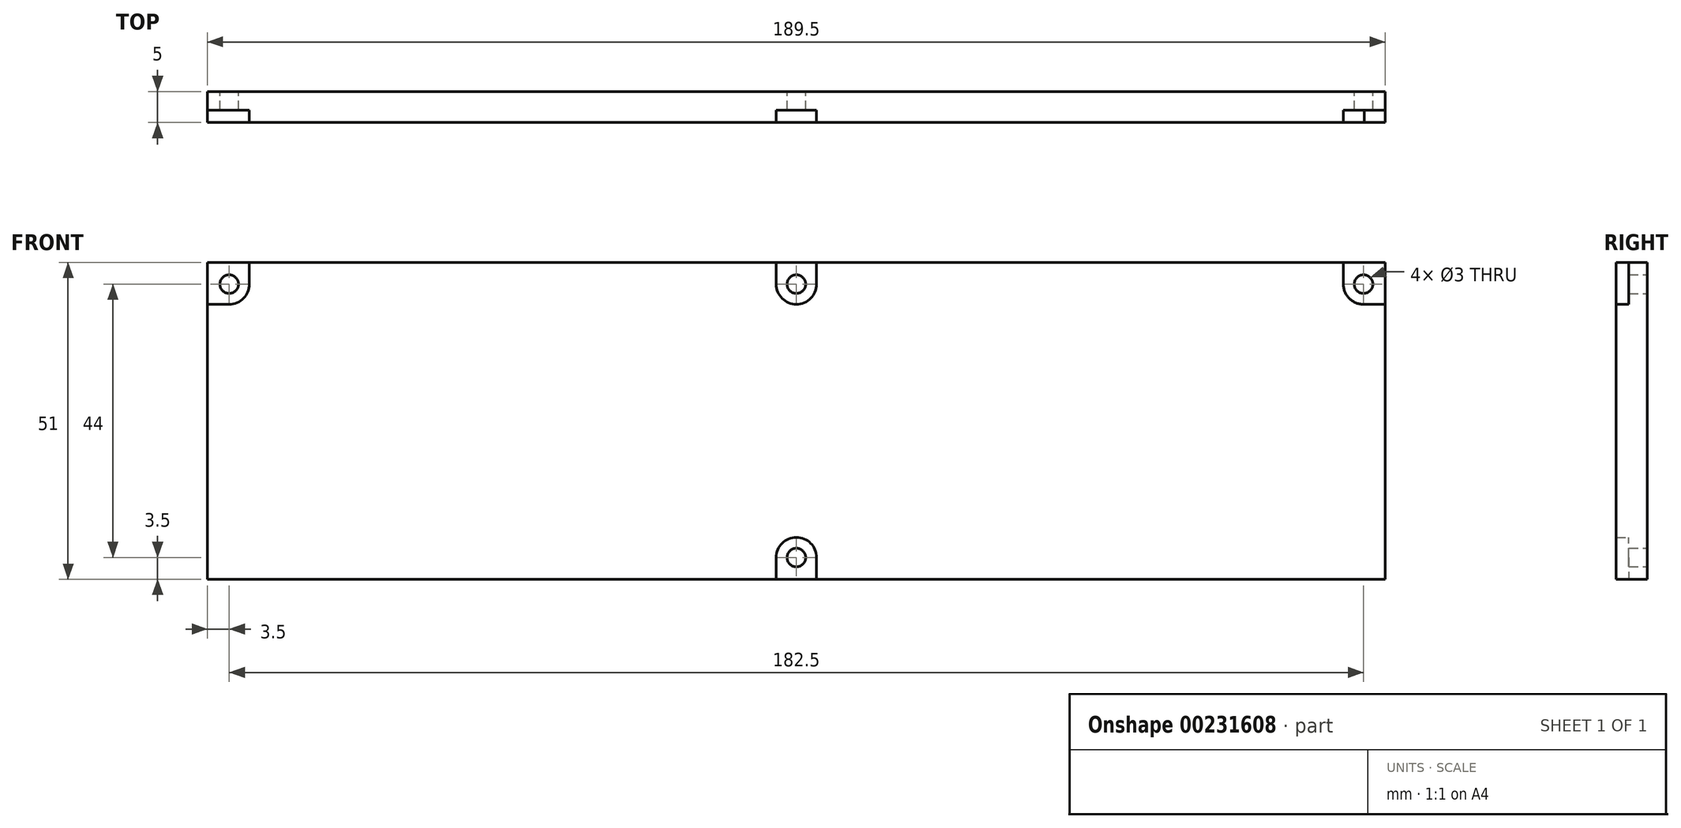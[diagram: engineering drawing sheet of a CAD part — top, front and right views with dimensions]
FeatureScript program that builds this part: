
annotation { "Feature Type Name" : "Feature", "Feature Type Description" : "" }
export const myFeature = defineFeature(function(context is Context, id is Id, definition is map)
    precondition{}
    {
        {
            var Q0;
            Q0=qCreatedBy(makeId("Front.planeOp"),FACE);
            var sketch = newSketch(context, id + "F0", { "sketchPlane" : qUnion([Q0])});
            skLineSegment(sketch, "E0.bottom", {"start": v(0, 0) * mm, "end": v(189.5, 0) * mm});
            skLineSegment(sketch, "E0.top", {"start": v(0, 51) * mm, "end": v(189.5, 51) * mm});
            skLineSegment(sketch, "E0.left", {"start": v(0, 0) * mm, "end": v(0, 51) * mm});
            skLineSegment(sketch, "E0.right", {"start": v(189.5, 0) * mm, "end": v(189.5, 51) * mm});
            skLineSegment(sketch, "E1", {"start": v(0, 3.5) * mm, "end": v(189.5, 3.5) * mm, "construction": true});
            skCircle(sketch, "E2", {"center": v(94.75, 3.5) * mm, "radius": 1.5 * mm});
            skArc(sketch, "E3", {"start": v(98, 3.5) * mm, "mid": v(94.75, 6.75) * mm, "end": v(91.5, 3.5) * mm});
            skLineSegment(sketch, "E4", {"start": v(98, 3.5) * mm, "end": v(98, 0) * mm});
            skLineSegment(sketch, "E5", {"start": v(91.5, 3.5) * mm, "end": v(91.5, 0) * mm});
            skLineSegment(sketch, "E6", {"start": v(0, 47.5) * mm, "end": v(189.5, 47.5) * mm, "construction": true});
            skCircle(sketch, "E7", {"center": v(94.75, 47.5) * mm, "radius": 1.5 * mm});
            skCircle(sketch, "E8", {"center": v(186, 47.5) * mm, "radius": 1.5 * mm});
            skCircle(sketch, "E9", {"center": v(3.5, 47.5) * mm, "radius": 1.5 * mm});
            skArc(sketch, "E10", {"start": v(182.75, 47.5) * mm, "mid": v(183.75, 45.16) * mm, "end": v(186.13, 44.25) * mm});
            skArc(sketch, "E11", {"start": v(91.5, 47.5) * mm, "mid": v(94.75, 44.25) * mm, "end": v(98, 47.5) * mm});
            skArc(sketch, "E12", {"start": v(3.5, 44.25) * mm, "mid": v(5.8, 45.2) * mm, "end": v(6.75, 47.5) * mm});
            skLineSegment(sketch, "E13", {"start": v(6.75, 47.5) * mm, "end": v(6.75, 51) * mm});
            skLineSegment(sketch, "E14", {"start": v(3.5, 44.25) * mm, "end": v(0, 44.25) * mm});
            skLineSegment(sketch, "E15", {"start": v(91.5, 47.5) * mm, "end": v(91.5, 51) * mm});
            skLineSegment(sketch, "E16", {"start": v(98, 47.5) * mm, "end": v(98, 51) * mm});
            skLineSegment(sketch, "E17", {"start": v(182.75, 47.5) * mm, "end": v(182.75, 51) * mm});
            skLineSegment(sketch, "E18", {"start": v(185.87, 44.25) * mm, "end": v(189.5, 44.25) * mm});
            skSolve(sketch);
        }
        {
            var Q0;
            Q0=makeQuery(id+"F0.imprint","IMPRINT",FACE,{"disambiguationData":[TD([[makeQuery(id+"F0.imprint","IMPRINT",EDGE,{"derivedFrom":sQuery(id+"F0.wireOp",EDGE,"E0.bottom")}),1.0]])]});
            extrude(context, id + "F1", {"entities" : qUnion([Q0]), "depth" : 5 * mm});
        }
        {
            var Q0;
            Q0=makeQuery(id+"F1.opExtrude","SWEPT_FACE",FACE,{"disambiguationData":[OSD([sQuery(id+"F0.wireOp",EDGE,"E0.left")])]});
            var sketch = newSketch(context, id + "F2", { "sketchPlane" : qUnion([Q0])});
            skCircle(sketch, "E19", {"center": v(2.5, -24.5) * mm, "radius": 1.5 * mm});
            skSolve(sketch);
        }
        {
            var Q0;
            Q0 = qSketchRegion(id + "F2", true);
            extrude(context, id + "F3", {"entities" : qUnion([Q0]), "operationType" : NewBodyOperationType.REMOVE, "oppositeDirection" : true, "depth" : 5 * mm});
        }
        {
            var Q0;
            Q0=makeQuery(id+"F0.imprint","IMPRINT",FACE,{"disambiguationData":[TD([[makeQuery(id+"F0.imprint","IMPRINT",EDGE,{"derivedFrom":sQuery(id+"F0.wireOp",EDGE,"E9")}),-1.0]])]});
            var Q1;
            Q1=makeQuery(id+"F0.imprint","IMPRINT",FACE,{"disambiguationData":[TD([[makeQuery(id+"F0.imprint","IMPRINT",EDGE,{"derivedFrom":sQuery(id+"F0.wireOp",EDGE,"E7")}),-1.0]])]});
            var Q2;
            Q2=makeQuery(id+"F0.imprint","IMPRINT",FACE,{"disambiguationData":[TD([[makeQuery(id+"F0.imprint","IMPRINT",EDGE,{"derivedFrom":sQuery(id+"F0.wireOp",EDGE,"E8")}),-1.0]])]});
            var Q3;
            Q3=makeQuery(id+"F0.imprint","IMPRINT",FACE,{"disambiguationData":[TD([[makeQuery(id+"F0.imprint","IMPRINT",EDGE,{"derivedFrom":sQuery(id+"F0.wireOp",EDGE,"E2")}),-1.0]])]});
            extrude(context, id + "F4", {"entities" : qUnion([Q0, Q1, Q2, Q3]), "operationType" : NewBodyOperationType.ADD, "depth" : 3 * mm});
        }
        {
            var Q0;
            Q0=makeQuery(id+"F1.opExtrude","SWEPT_FACE",FACE,{"disambiguationData":[OSD([sQuery(id+"F0.wireOp",EDGE,"E0.right")])]});
            var sketch = newSketch(context, id + "F5", { "sketchPlane" : qUnion([Q0])});
            skCircle(sketch, "E20", {"center": v(-2.5, -24.5) * mm, "radius": 1.5 * mm});
            skSolve(sketch);
        }
        {
            var Q0;
            Q0=makeQuery(id+"F5.imprint","IMPRINT",FACE,{"disambiguationData":[TD([[makeQuery(id+"F5.imprint","IMPRINT",EDGE,{"derivedFrom":sQuery(id+"F5.wireOp",EDGE,"E20")}),1.0]])]});
            extrude(context, id + "F6", {"entities" : qUnion([Q0]), "operationType" : NewBodyOperationType.REMOVE, "oppositeDirection" : true, "depth" : 5 * mm});
        }
    });
